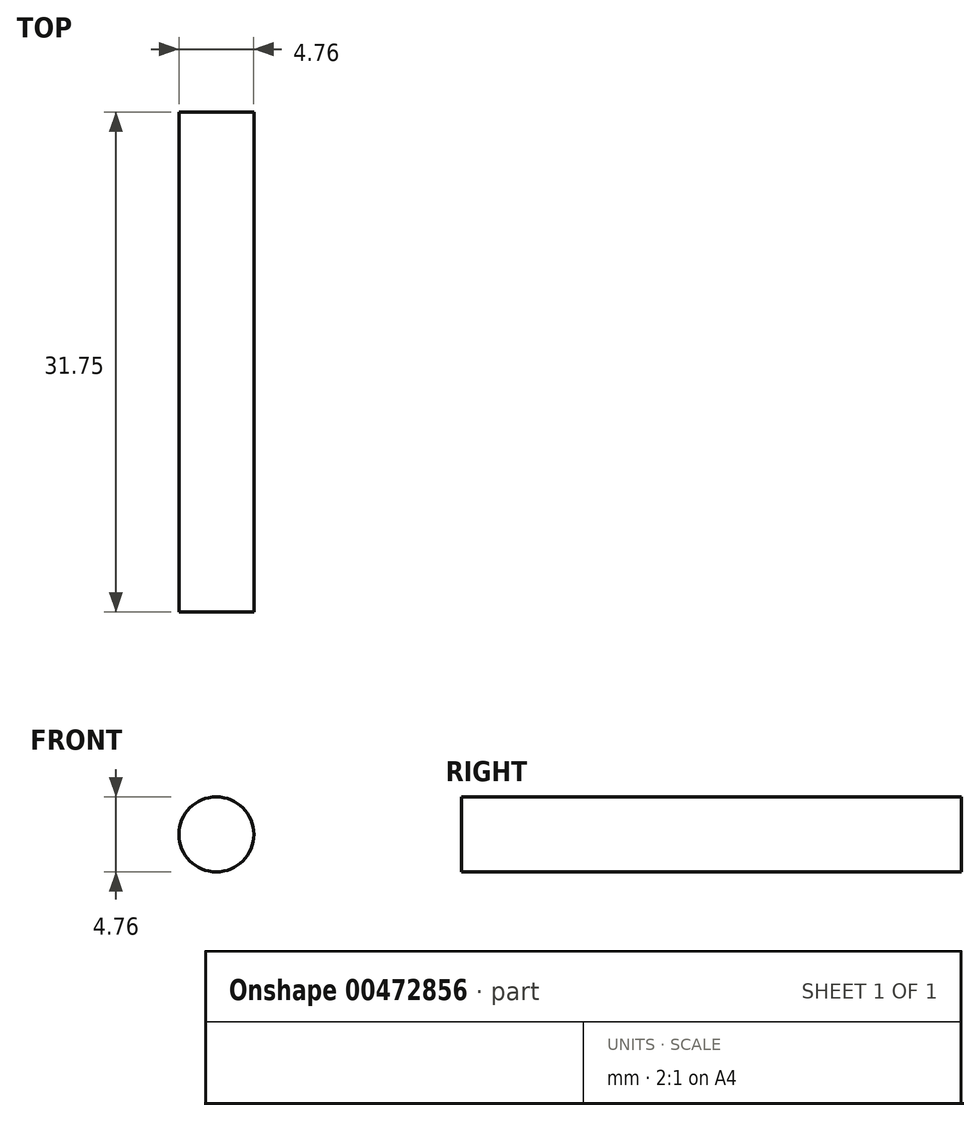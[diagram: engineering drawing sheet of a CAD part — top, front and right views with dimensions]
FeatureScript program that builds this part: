
annotation { "Feature Type Name" : "Feature", "Feature Type Description" : "" }
export const myFeature = defineFeature(function(context is Context, id is Id, definition is map)
    precondition{}
    {
        {
            var Q0;
            Q0=qCreatedBy(makeId("Front.planeOp"),FACE);
            var sketch = newSketch(context, id + "F0", { "sketchPlane" : qUnion([Q0])});
            skCircle(sketch, "E0", {"center": v(0, 0) * mm, "radius": 2.38 * mm});
            skSolve(sketch);
        }
        {
            var Q0;
            Q0=makeQuery(id+"F0.imprint","IMPRINT",FACE,{"disambiguationData":[TD([[makeQuery(id+"F0.imprint","IMPRINT",EDGE,{"derivedFrom":sQuery(id+"F0.wireOp",EDGE,"E0")}),1.0]])]});
            extrude(context, id + "F1", {"entities" : qUnion([Q0]), "depth" : 31.75 * mm});
        }
    });
